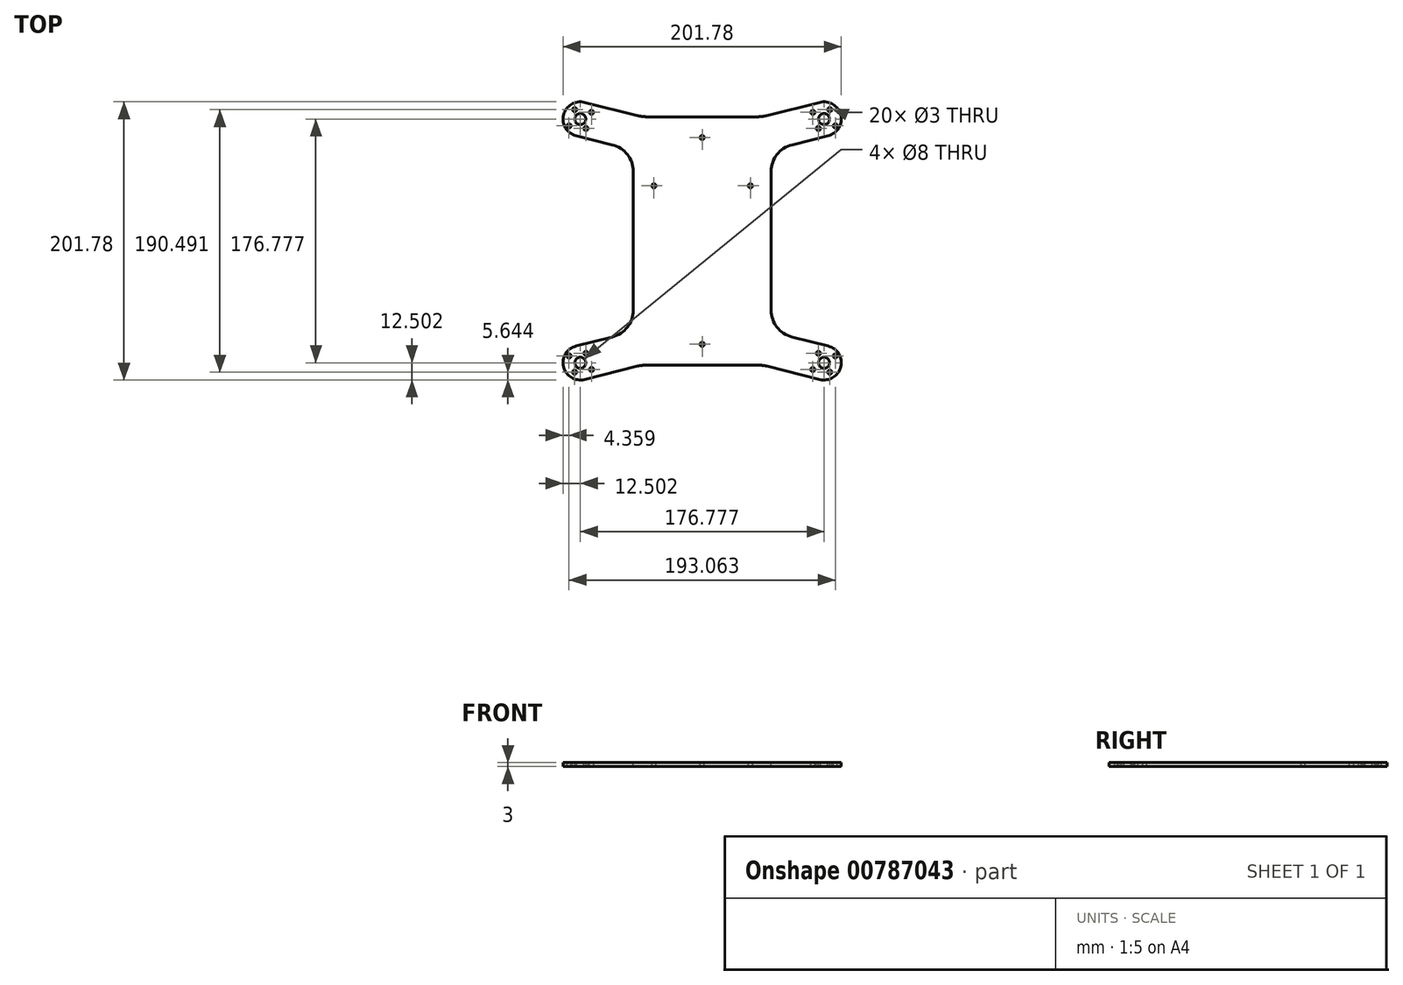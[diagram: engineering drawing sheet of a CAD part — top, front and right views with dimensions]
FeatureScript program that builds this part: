
annotation { "Feature Type Name" : "Feature", "Feature Type Description" : "" }
export const myFeature = defineFeature(function(context is Context, id is Id, definition is map)
    precondition{}
    {
        {
            var Q0;
            Q0=qCreatedBy(makeId("Top.planeOp"),FACE);
            var sketch = newSketch(context, id + "F0", { "sketchPlane" : qUnion([Q0])});
            skLineSegment(sketch, "E0.bottom", {"start": v(-39.5, 90) * mm, "end": v(0, 90) * mm});
            skLineSegment(sketch, "E0.top", {"start": v(-50, 0) * mm, "end": v(0, 0) * mm});
            skLineSegment(sketch, "E0.left", {"start": v(-50, 50.3) * mm, "end": v(-50, 0) * mm});
            skCircle(sketch, "E1", {"center": v(0, 0) * mm, "radius": 125 * mm, "construction": true});
            skPoint(sketch, "E2", {"position": v(-88.39, 88.39) * mm});
            skLineSegment(sketch, "E3.bottom", {"start": v(-88.39, 88.39) * mm, "end": v(88.39, 88.39) * mm, "construction": true});
            skLineSegment(sketch, "E3.left", {"start": v(-88.39, 88.39) * mm, "end": v(-88.39, -88.39) * mm, "construction": true});
            skLineSegment(sketch, "E3.right", {"start": v(88.39, 88.39) * mm, "end": v(88.39, -88.39) * mm, "construction": true});
            skLineSegment(sketch, "E4", {"start": v(-88.39, 88.39) * mm, "end": v(0, 66.35) * mm, "construction": true});
            skLineSegment(sketch, "E5", {"start": v(-91.41, 76.26) * mm, "end": v(-65.16, 69.71) * mm});
            skLineSegment(sketch, "E6", {"start": v(-85.36, 100.52) * mm, "end": v(-46.76, 90.9) * mm});
            skArc(sketch, "E7.filletArc", {"start": v(-50, 50.3) * mm, "mid": v(-54.24, 62.62) * mm, "end": v(-65.16, 69.71) * mm});
            skPoint(sketch, "E8.newPointB", {"position": v(-50, 90) * mm});
            skArc(sketch, "E8.filletArc", {"start": v(-46.76, 90.9) * mm, "mid": v(-43.16, 90.22) * mm, "end": v(-39.5, 90) * mm});
            skArc(sketch, "E9.trimOffspring", {"start": v(-85.36, 100.52) * mm, "mid": v(-100.52, 91.41) * mm, "end": v(-91.41, 76.26) * mm});
            skLineSegment(sketch, "E10", {"start": v(-94.64, 98.8) * mm, "end": v(-82.13, 77.98) * mm, "construction": true});
            skLineSegment(sketch, "E11", {"start": v(-103.77, 79.15) * mm, "end": v(-73, 97.63) * mm, "construction": true});
            skPoint(sketch, "E12", {"position": v(-80.25, 93.28) * mm});
            skPoint(sketch, "E13", {"position": v(-92.5, 95.25) * mm});
            skPoint(sketch, "E14", {"position": v(-96.53, 83.5) * mm});
            skPoint(sketch, "E15", {"position": v(-84.27, 81.53) * mm});
            skCircle(sketch, "E16", {"center": v(-88.39, 88.39) * mm, "radius": 9.5 * mm, "construction": true});
            skCircle(sketch, "E17", {"center": v(-88.39, 88.39) * mm, "radius": 8 * mm, "construction": true});
            skLineSegment(sketch, "E18.MirrorCS", {"start": v(0, 90) * mm, "end": v(0, 0) * mm});
            skLineSegment(sketch, "E19.MirrorCS", {"start": v(-88.39, -88.39) * mm, "end": v(88.39, -88.39) * mm, "construction": true});
            skPoint(sketch, "E20", {"position": v(0, 75) * mm});
            skPoint(sketch, "E21", {"position": v(-35, 40) * mm});
            skCircle(sketch, "E22", {"center": v(-88.39, 88.39) * mm, "radius": 4 * mm});
            skCircle(sketch, "E23", {"center": v(-80.25, 93.28) * mm, "radius": 1.5 * mm});
            skCircle(sketch, "E24", {"center": v(-92.5, 95.25) * mm, "radius": 1.5 * mm});
            skCircle(sketch, "E25", {"center": v(-96.53, 83.5) * mm, "radius": 1.5 * mm});
            skCircle(sketch, "E26", {"center": v(-84.27, 81.53) * mm, "radius": 1.5 * mm});
            skArc(sketch, "E27.MirrorCS", {"start": v(46.76, 90.9) * mm, "mid": v(43.16, 90.22) * mm, "end": v(39.5, 90) * mm});
            skCircle(sketch, "E28.MirrorC", {"center": v(80.25, 93.28) * mm, "radius": 1.5 * mm});
            skCircle(sketch, "E29.MirrorC", {"center": v(92.5, 95.25) * mm, "radius": 1.5 * mm});
            skCircle(sketch, "E30.MirrorC", {"center": v(84.27, 81.53) * mm, "radius": 1.5 * mm});
            skCircle(sketch, "E31.MirrorC", {"center": v(96.53, 83.5) * mm, "radius": 1.5 * mm});
            skLineSegment(sketch, "E32.MirrorCS", {"start": v(94.64, 98.8) * mm, "end": v(82.13, 77.98) * mm, "construction": true});
            skLineSegment(sketch, "E33.MirrorCS", {"start": v(88.39, 88.39) * mm, "end": v(0, 66.35) * mm, "construction": true});
            skLineSegment(sketch, "E34.MirrorCS", {"start": v(103.77, 79.15) * mm, "end": v(73, 97.63) * mm, "construction": true});
            skCircle(sketch, "E35.MirrorC", {"center": v(88.39, 88.39) * mm, "radius": 4 * mm});
            skCircle(sketch, "E36.MirrorC", {"center": v(88.39, 88.39) * mm, "radius": 9.5 * mm, "construction": true});
            skLineSegment(sketch, "E37.MirrorCS", {"start": v(91.41, 76.26) * mm, "end": v(65.16, 69.71) * mm});
            skCircle(sketch, "E38.MirrorC", {"center": v(88.39, 88.39) * mm, "radius": 8 * mm, "construction": true});
            skArc(sketch, "E39.MirrorCS", {"start": v(50, 50.3) * mm, "mid": v(54.24, 62.62) * mm, "end": v(65.16, 69.71) * mm});
            skPoint(sketch, "E40.MirrorP", {"position": v(50, 90) * mm});
            skLineSegment(sketch, "E41.MirrorCS", {"start": v(50, 50.3) * mm, "end": v(50, 0) * mm});
            skArc(sketch, "E42.MirrorCS", {"start": v(85.36, 100.52) * mm, "mid": v(100.52, 91.41) * mm, "end": v(91.41, 76.26) * mm});
            skLineSegment(sketch, "E43.MirrorCS", {"start": v(50, 0) * mm, "end": v(0, 0) * mm});
            skLineSegment(sketch, "E44.MirrorCS", {"start": v(85.36, 100.52) * mm, "end": v(46.76, 90.9) * mm});
            skLineSegment(sketch, "E45.MirrorCS", {"start": v(39.5, 90) * mm, "end": v(0, 90) * mm});
            skCircle(sketch, "E46.MirrorC", {"center": v(80.25, -93.28) * mm, "radius": 1.5 * mm});
            skCircle(sketch, "E47.MirrorC", {"center": v(92.5, -95.25) * mm, "radius": 1.5 * mm});
            skCircle(sketch, "E48.MirrorC", {"center": v(-80.25, -93.28) * mm, "radius": 1.5 * mm});
            skCircle(sketch, "E49.MirrorC", {"center": v(84.27, -81.53) * mm, "radius": 1.5 * mm});
            skCircle(sketch, "E50.MirrorC", {"center": v(-84.27, -81.53) * mm, "radius": 1.5 * mm});
            skArc(sketch, "E51.MirrorCS", {"start": v(-46.76, -90.9) * mm, "mid": v(-43.16, -90.22) * mm, "end": v(-39.5, -90) * mm});
            skCircle(sketch, "E52.MirrorC", {"center": v(-96.53, -83.5) * mm, "radius": 1.5 * mm});
            skLineSegment(sketch, "E53.MirrorCS", {"start": v(-94.64, -98.8) * mm, "end": v(-82.13, -77.98) * mm, "construction": true});
            skLineSegment(sketch, "E54.MirrorCS", {"start": v(94.64, -98.8) * mm, "end": v(82.13, -77.98) * mm, "construction": true});
            skCircle(sketch, "E55.MirrorC", {"center": v(-92.5, -95.25) * mm, "radius": 1.5 * mm});
            skArc(sketch, "E56.MirrorCS", {"start": v(46.76, -90.9) * mm, "mid": v(43.16, -90.22) * mm, "end": v(39.5, -90) * mm});
            skCircle(sketch, "E57.MirrorC", {"center": v(96.53, -83.5) * mm, "radius": 1.5 * mm});
            skLineSegment(sketch, "E58.MirrorCS", {"start": v(0, -90) * mm, "end": v(0, 0) * mm});
            skLineSegment(sketch, "E59.MirrorCS", {"start": v(-103.77, -79.15) * mm, "end": v(-73, -97.63) * mm, "construction": true});
            skCircle(sketch, "E60.MirrorC", {"center": v(88.39, -88.39) * mm, "radius": 4 * mm});
            skLineSegment(sketch, "E61.MirrorCS", {"start": v(103.77, -79.15) * mm, "end": v(73, -97.63) * mm, "construction": true});
            skCircle(sketch, "E62.MirrorC", {"center": v(-88.39, -88.39) * mm, "radius": 4 * mm});
            skLineSegment(sketch, "E63.MirrorCS", {"start": v(-85.36, -100.52) * mm, "end": v(-46.76, -90.9) * mm});
            skLineSegment(sketch, "E64.MirrorCS", {"start": v(85.36, -100.52) * mm, "end": v(46.76, -90.9) * mm});
            skArc(sketch, "E65.MirrorCS", {"start": v(85.36, -100.52) * mm, "mid": v(100.52, -91.41) * mm, "end": v(91.41, -76.26) * mm});
            skArc(sketch, "E66.MirrorCS", {"start": v(-50, -50.3) * mm, "mid": v(-54.24, -62.62) * mm, "end": v(-65.16, -69.71) * mm});
            skArc(sketch, "E67.MirrorCS", {"start": v(50, -50.3) * mm, "mid": v(54.24, -62.62) * mm, "end": v(65.16, -69.71) * mm});
            skCircle(sketch, "E68.MirrorC", {"center": v(88.39, -88.39) * mm, "radius": 8 * mm, "construction": true});
            skLineSegment(sketch, "E69.MirrorCS", {"start": v(-39.5, -90) * mm, "end": v(0, -90) * mm});
            skPoint(sketch, "E70.MirrorP", {"position": v(-50, -90) * mm});
            skLineSegment(sketch, "E71.MirrorCS", {"start": v(39.5, -90) * mm, "end": v(0, -90) * mm});
            skLineSegment(sketch, "E72.MirrorCS", {"start": v(88.39, -88.39) * mm, "end": v(0, -66.35) * mm, "construction": true});
            skLineSegment(sketch, "E73.MirrorCS", {"start": v(-88.39, -88.39) * mm, "end": v(0, -66.35) * mm, "construction": true});
            skLineSegment(sketch, "E74.MirrorCS", {"start": v(-91.41, -76.26) * mm, "end": v(-65.16, -69.71) * mm});
            skLineSegment(sketch, "E75.MirrorCS", {"start": v(50, -50.3) * mm, "end": v(50, 0) * mm});
            skLineSegment(sketch, "E76.MirrorCS", {"start": v(91.41, -76.26) * mm, "end": v(65.16, -69.71) * mm});
            skCircle(sketch, "E77.MirrorC", {"center": v(-88.39, -88.39) * mm, "radius": 9.5 * mm, "construction": true});
            skArc(sketch, "E78.MirrorCS", {"start": v(-85.36, -100.52) * mm, "mid": v(-100.52, -91.41) * mm, "end": v(-91.41, -76.26) * mm});
            skLineSegment(sketch, "E79.MirrorCS", {"start": v(-50, -50.3) * mm, "end": v(-50, 0) * mm});
            skCircle(sketch, "E80.MirrorC", {"center": v(-88.39, -88.39) * mm, "radius": 8 * mm, "construction": true});
            skPoint(sketch, "E81.MirrorP", {"position": v(50, -90) * mm});
            skCircle(sketch, "E82.MirrorC", {"center": v(88.39, -88.39) * mm, "radius": 9.5 * mm, "construction": true});
            skCircle(sketch, "E83", {"center": v(-35, 40) * mm, "radius": 1.5 * mm});
            skCircle(sketch, "E84", {"center": v(0, 75) * mm, "radius": 1.5 * mm});
            skCircle(sketch, "E85.MirrorC", {"center": v(35, 40) * mm, "radius": 1.5 * mm});
            skCircle(sketch, "E86.MirrorC", {"center": v(0, -75) * mm, "radius": 1.5 * mm});
            skSolve(sketch);
        }
        {
            var Q0;
            Q0 = qSketchRegion(id + "F0", true);
            extrude(context, id + "F1", {"entities" : qUnion([Q0]), "oppositeDirection" : true, "depth" : 3 * mm, "offsetDistance" : 25 * mm});
        }
    });
